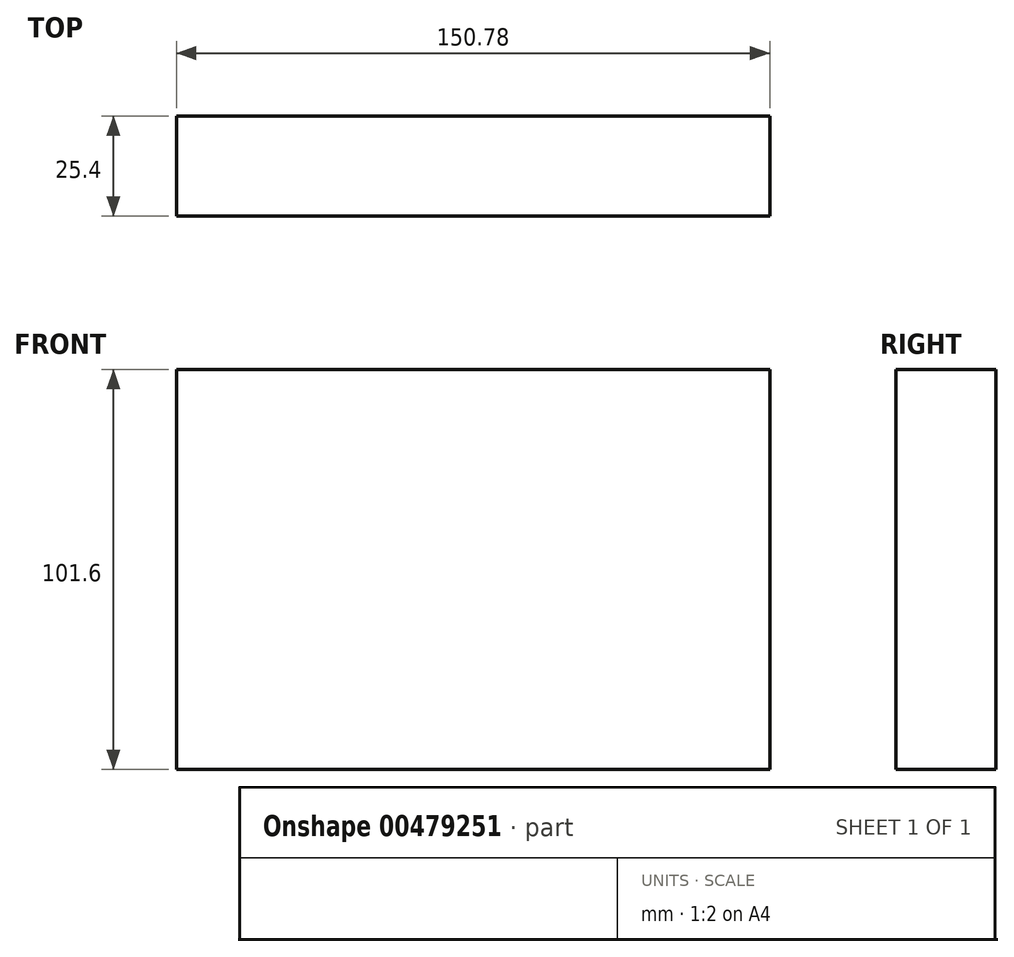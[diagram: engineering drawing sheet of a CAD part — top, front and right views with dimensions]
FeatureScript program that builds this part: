
annotation { "Feature Type Name" : "Feature", "Feature Type Description" : "" }
export const myFeature = defineFeature(function(context is Context, id is Id, definition is map)
    precondition{}
    {
        {
            var Q0;
            Q0=qCreatedBy(makeId("Top.planeOp"),FACE);
            var sketch = newSketch(context, id + "F0", { "sketchPlane" : qUnion([Q0])});
            skLineSegment(sketch, "E0.bottom", {"start": v(-74.8, -54.7) * mm, "end": v(75.99, -54.7) * mm});
            skLineSegment(sketch, "E0.top", {"start": v(-74.8, 50.06) * mm, "end": v(75.99, 50.06) * mm});
            skLineSegment(sketch, "E0.left", {"start": v(-74.8, -54.7) * mm, "end": v(-74.8, 50.06) * mm});
            skLineSegment(sketch, "E0.right", {"start": v(75.99, -54.7) * mm, "end": v(75.99, 50.06) * mm});
            skSolve(sketch);
        }
        {
            var Q0;
            Q0=makeQuery(id+"F0.imprint","IMPRINT",FACE,{"disambiguationData":[TD([[makeQuery(id+"F0.imprint","IMPRINT",EDGE,{"derivedFrom":sQuery(id+"F0.wireOp",EDGE,"E0.bottom")}),1.0]])]});
            var Q1;
            Q1=sQuery(id+"F0.wireOp",EDGE,"E0.top");
            var Q2;
            Q2=sQuery(id+"F0.wireOp",EDGE,"E0.left");
            var Q3;
            Q3=sQuery(id+"F0.wireOp",EDGE,"E0.bottom");
            var Q4;
            Q4=sQuery(id+"F0.wireOp",EDGE,"E0.right");
            extrude(context, id + "F1", {"entities" : qUnion([Q0]), "bodyType" : ToolBodyType.SURFACE, "surfaceEntities" : qUnion([Q1, Q2, Q3, Q4]), "endBound" : BoundingType.SYMMETRIC, "depth" : 101.6 * mm});
        }
        {
            var Q0;
            Q0=makeQuery(id+"F1.opExtrude","SWEPT_FACE",FACE,{"disambiguationData":[OSD([sQuery(id+"F0.wireOp",EDGE,"E0.bottom")])]});
            extrude(context, id + "F2", {"entities" : qUnion([Q0]), "depth" : 25.4 * mm});
        }
    });
